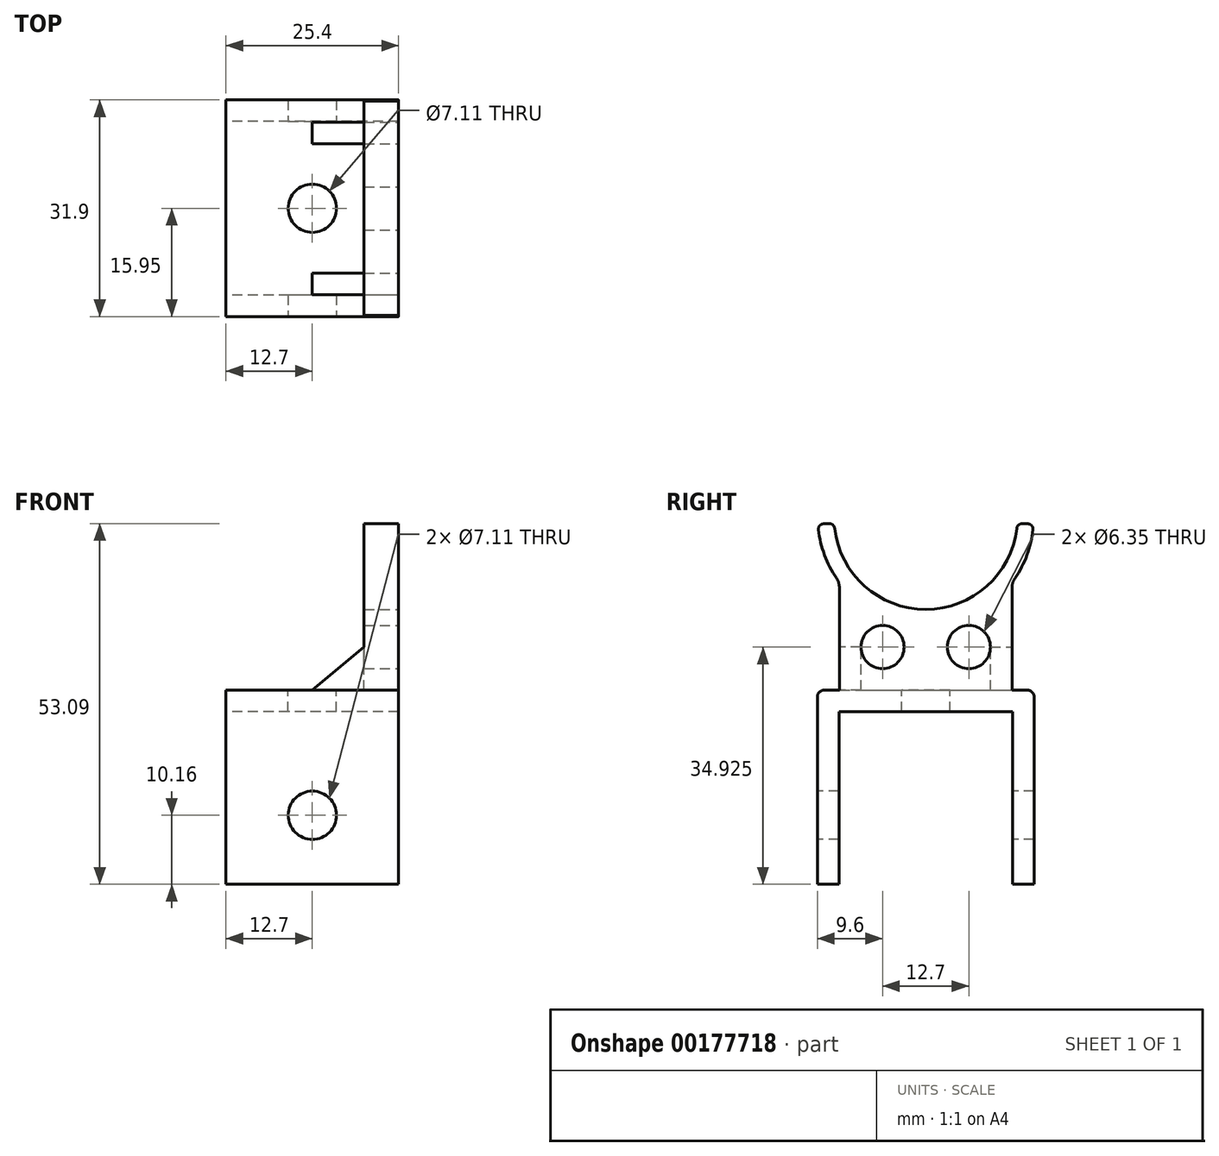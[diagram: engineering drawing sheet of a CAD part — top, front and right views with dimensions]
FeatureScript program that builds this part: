
annotation { "Feature Type Name" : "Feature", "Feature Type Description" : "" }
export const myFeature = defineFeature(function(context is Context, id is Id, definition is map)
    precondition{}
    {
        {
            var Q0;
            Q0=qCreatedBy(makeId("Right.planeOp"),FACE);
            var sketch = newSketch(context, id + "F0", { "sketchPlane" : qUnion([Q0])});
            skLineSegment(sketch, "E0.bottom", {"start": v(-12.78, 12.7) * mm, "end": v(12.78, 12.7) * mm});
            skLineSegment(sketch, "E0.left", {"start": v(-12.78, 12.7) * mm, "end": v(-12.78, -12.7) * mm});
            skLineSegment(sketch, "E0.right", {"start": v(12.78, 12.7) * mm, "end": v(12.78, -12.7) * mm});
            skLineSegment(sketch, "E1.0", {"start": v(15.95, 15.88) * mm, "end": v(15.95, -12.7) * mm});
            skLineSegment(sketch, "E2.0", {"start": v(-15.95, 15.87) * mm, "end": v(15.95, 15.88) * mm});
            skLineSegment(sketch, "E3.0", {"start": v(-15.95, 15.88) * mm, "end": v(-15.95, -12.7) * mm});
            skLineSegment(sketch, "E4", {"start": v(-15.95, -12.7) * mm, "end": v(-12.78, -12.7) * mm});
            skLineSegment(sketch, "E5", {"start": v(12.78, -12.7) * mm, "end": v(15.95, -12.7) * mm});
            skSolve(sketch);
        }
        {
            var Q0;
            Q0=makeQuery(id+"F0.imprint","IMPRINT",FACE,{"disambiguationData":[TD([[makeQuery(id+"F0.imprint","IMPRINT",EDGE,{"derivedFrom":sQuery(id+"F0.wireOp",EDGE,"E0.bottom")}),1.0]])]});
            extrude(context, id + "F1", {"entities" : qUnion([Q0]), "depth" : 25.4 * mm});
        }
        {
            var Q0;
            Q0=makeQuery(id+"F1.opExtrude","CAP_FACE",FACE,{"disambiguationData":[OSD([sQuery(id+"F0.wireOp",EDGE,"E0.bottom"),sQuery(id+"F0.wireOp",EDGE,"E0.left"),sQuery(id+"F0.wireOp",EDGE,"E0.right"),sQuery(id+"F0.wireOp",EDGE,"E1.0"),sQuery(id+"F0.wireOp",EDGE,"E2.0"),sQuery(id+"F0.wireOp",EDGE,"E3.0"),sQuery(id+"F0.wireOp",EDGE,"E4"),sQuery(id+"F0.wireOp",EDGE,"E5")])],"isStart":false});
            cPlane(context, id + "F2", {"entities" : qUnion([Q0]), "cplaneType" : CPlaneType.OFFSET, "offset" : 0 * mm, "width" : 152.4 * mm, "height" : 152.4 * mm});
        }
        {
            var Q0;
            Q0=qCreatedBy(id+"F2.planeOp",FACE);
            var sketch = newSketch(context, id + "F3", { "sketchPlane" : qUnion([Q0])});
            skPoint(sketch, "E6.0", {"position": v(0, 15.88) * mm});
            skLineSegment(sketch, "E7", {"start": v(0, 15.88) * mm, "end": v(0, 41.28) * mm, "construction": true});
            skArc(sketch, "E8", {"start": v(-13.4, 39.72) * mm, "mid": v(-8.98, 31.2) * mm, "end": v(0, 27.78) * mm});
            skLineSegment(sketch, "E9", {"start": v(-15.04, 40.37) * mm, "end": v(-14.18, 40.4) * mm});
            skPoint(sketch, "E10.visualSharp", {"position": v(-15.85, 40.36) * mm});
            skArc(sketch, "E10.filletArc", {"start": v(-15.04, 40.37) * mm, "mid": v(-15.6, 40.11) * mm, "end": v(-15.78, 39.53) * mm});
            skPoint(sketch, "E11.visualSharp", {"position": v(-13.47, 40.4) * mm});
            skArc(sketch, "E11.filletArc", {"start": v(-13.4, 39.72) * mm, "mid": v(-13.67, 40.2) * mm, "end": v(-14.18, 40.4) * mm});
            skLineSegment(sketch, "E12", {"start": v(-12.7, 15.88) * mm, "end": v(-12.7, 30.94) * mm});
            skArc(sketch, "E13", {"start": v(-15.78, 39.53) * mm, "mid": v(-14.9, 35.78) * mm, "end": v(-13.14, 32.36) * mm});
            skArc(sketch, "E14.MirrorCS", {"start": v(13.4, 39.72) * mm, "mid": v(8.98, 31.2) * mm, "end": v(0, 27.78) * mm});
            skLineSegment(sketch, "E15.MirrorCS", {"start": v(12.7, 15.88) * mm, "end": v(12.7, 30.94) * mm});
            skLineSegment(sketch, "E16.MirrorCS", {"start": v(15.04, 40.37) * mm, "end": v(14.18, 40.4) * mm});
            skArc(sketch, "E17.MirrorCS", {"start": v(13.4, 39.72) * mm, "mid": v(13.67, 40.2) * mm, "end": v(14.18, 40.4) * mm});
            skArc(sketch, "E18.MirrorCS", {"start": v(15.04, 40.37) * mm, "mid": v(15.6, 40.11) * mm, "end": v(15.78, 39.53) * mm});
            skArc(sketch, "E19.MirrorCS", {"start": v(15.78, 39.53) * mm, "mid": v(14.9, 35.78) * mm, "end": v(13.14, 32.36) * mm});
            skPoint(sketch, "E20.MirrorP", {"position": v(13.47, 40.4) * mm});
            skPoint(sketch, "E21.MirrorP", {"position": v(15.85, 40.36) * mm});
            skLineSegment(sketch, "E22", {"start": v(-12.7, 15.88) * mm, "end": v(12.7, 15.88) * mm});
            skPoint(sketch, "E23.visualSharp", {"position": v(-12.7, 31.75) * mm});
            skArc(sketch, "E23.filletArc", {"start": v(-12.7, 30.94) * mm, "mid": v(-12.81, 31.68) * mm, "end": v(-13.14, 32.36) * mm});
            skPoint(sketch, "E24.visualSharp", {"position": v(12.7, 31.75) * mm});
            skArc(sketch, "E24.filletArc", {"start": v(13.14, 32.36) * mm, "mid": v(12.81, 31.68) * mm, "end": v(12.7, 30.94) * mm});
            skCircle(sketch, "E25", {"center": v(-6.35, 22.23) * mm, "radius": 3.18 * mm});
            skCircle(sketch, "E26.MirrorC", {"center": v(6.35, 22.23) * mm, "radius": 3.18 * mm});
            skSolve(sketch);
        }
        {
            var Q0;
            Q0=makeQuery(id+"F3.imprint","IMPRINT",FACE,{"disambiguationData":[TD([[makeQuery(id+"F3.imprint","IMPRINT",EDGE,{"derivedFrom":sQuery(id+"F3.wireOp",EDGE,"E8")}),-1.0]])]});
            extrude(context, id + "F4", {"entities" : qUnion([Q0]), "operationType" : NewBodyOperationType.ADD, "oppositeDirection" : true, "depth" : 5.08 * mm});
        }
        {
            var Q0;
            Q0=makeQuery(id+"F1.opExtrude","SWEPT_FACE",FACE,{"disambiguationData":[OSD([sQuery(id+"F0.wireOp",EDGE,"E2.0")])]});
            cPlane(context, id + "F5", {"entities" : qUnion([Q0]), "cplaneType" : CPlaneType.OFFSET, "offset" : 0 * mm, "width" : 152.4 * mm, "height" : 152.4 * mm});
        }
        {
            var Q0;
            Q0=qCreatedBy(id+"F5.planeOp",FACE);
            var sketch = newSketch(context, id + "F6", { "sketchPlane" : qUnion([Q0])});
            skCircle(sketch, "E27", {"center": v(12.7, 0) * mm, "radius": 3.56 * mm});
            skSolve(sketch);
        }
        {
            var Q0;
            Q0 = qSketchRegion(id + "F6", true);
            extrude(context, id + "F7", {"entities" : qUnion([Q0]), "operationType" : NewBodyOperationType.REMOVE, "oppositeDirection" : true, "depth" : 6.35 * mm});
        }
        {
            var Q0;
            Q0=makeQuery(id+"F1.opExtrude","SWEPT_FACE",FACE,{"disambiguationData":[OSD([sQuery(id+"F0.wireOp",EDGE,"E3.0")])]});
            cPlane(context, id + "F8", {"entities" : qUnion([Q0]), "cplaneType" : CPlaneType.OFFSET, "offset" : 0 * mm, "width" : 152.4 * mm, "height" : 152.4 * mm});
        }
        {
            var Q0;
            Q0=qCreatedBy(id+"F8.planeOp",FACE);
            var sketch = newSketch(context, id + "F9", { "sketchPlane" : qUnion([Q0])});
            skCircle(sketch, "E28", {"center": v(12.7, -2.54) * mm, "radius": 3.56 * mm});
            skSolve(sketch);
        }
        {
            var Q0;
            Q0 = qSketchRegion(id + "F9", true);
            extrude(context, id + "F10", {"entities" : qUnion([Q0]), "operationType" : NewBodyOperationType.REMOVE, "endBound" : BoundingType.THROUGH_ALL, "oppositeDirection" : true, "depth" : 25.4 * mm});
        }
        {
            var Q0;
            Q0=makeQuery(id+"F4.opExtrude","SWEPT_FACE",FACE,{"disambiguationData":[OSD([sQuery(id+"F3.wireOp",EDGE,"E12")])]});
            cPlane(context, id + "F11", {"entities" : qUnion([Q0]), "cplaneType" : CPlaneType.OFFSET, "offset" : 0 * mm, "width" : 152.4 * mm, "height" : 152.4 * mm});
        }
        {
            var Q0;
            Q0=qCreatedBy(id+"F11.planeOp",FACE);
            var sketch = newSketch(context, id + "F12", { "sketchPlane" : qUnion([Q0])});
            skLineSegment(sketch, "E29.0", {"start": v(20.32, 15.88) * mm, "end": v(20.32, 30.94) * mm, "construction": true});
            skLineSegment(sketch, "E30", {"start": v(20.32, 15.88) * mm, "end": v(20.32, 22.23) * mm});
            skLineSegment(sketch, "E31", {"start": v(20.32, 15.88) * mm, "end": v(12.7, 15.88) * mm});
            skLineSegment(sketch, "E32", {"start": v(12.7, 15.88) * mm, "end": v(20.32, 22.23) * mm});
            skSolve(sketch);
        }
        {
            var Q0;
            Q0 = qSketchRegion(id + "F12", true);
            extrude(context, id + "F13", {"entities" : qUnion([Q0]), "oppositeDirection" : true, "depth" : 3.17 * mm});
        }
        {
            var Q0;
            Q0=makeQuery(id+"F13.opExtrude","SWEPT_BODY",BODY,{"disambiguationData":[OSD([sQuery(id+"F12.wireOp",EDGE,"E30"),sQuery(id+"F12.wireOp",EDGE,"E31"),sQuery(id+"F12.wireOp",EDGE,"E32")])]});
            var Q1;
            Q1=qCreatedBy(makeId("Front.planeOp"),FACE);
            mirror(context, id + "F14", {"operationType" : NewBodyOperationType.ADD, "entities" : qUnion([Q0]), "mirrorPlane" : qUnion([Q1])});
        }
        {
            var Q0;
            Q0=makeQuery(id+"F1.opExtrude","SWEPT_EDGE",EDGE,{"disambiguationData":[OSD([sQuery(id+"F0.wireOp",EDGE,"E2.0"),sQuery(id+"F0.wireOp",EDGE,"E3.0")])]});
            var Q1;
            Q1=makeQuery(id+"F1.opExtrude","SWEPT_EDGE",EDGE,{"disambiguationData":[OSD([sQuery(id+"F0.wireOp",EDGE,"E1.0"),sQuery(id+"F0.wireOp",EDGE,"E2.0")])]});
            var Q2;
            Q2=makeQuery(id+"F4.opExtrude","CAP_EDGE",EDGE,{"disambiguationData":[OSD([sQuery(id+"F3.wireOp",EDGE,"E22")])],"isStart":false});
            var Q3;
            Q3=makeQuery(id+"F14.opPattern","COPY",EDGE,{"derivedFrom":makeQuery(id+"F13.opExtrude","CAP_EDGE",EDGE,{"disambiguationData":[OSD([sQuery(id+"F12.wireOp",EDGE,"E31")])],"isStart":false}),"instanceName":"1"});
            var Q4;
            Q4=makeQuery(id+"F13.opExtrude","CAP_EDGE",EDGE,{"disambiguationData":[OSD([sQuery(id+"F12.wireOp",EDGE,"E31")])],"isStart":false});
            var Q5;
            Q5=makeQuery(id+"F14.boolean.opBoolean","MERGE",EDGE,{"derivedFrom":[makeQuery(id+"F4.opExtrude","SWEPT_EDGE",EDGE,{"disambiguationData":[OSD([sQuery(id+"F3.wireOp",EDGE,"E15.MirrorCS"),sQuery(id+"F3.wireOp",EDGE,"E22")])]}),makeQuery(id+"F14.opPattern","COPY",EDGE,{"derivedFrom":makeQuery(id+"F13.opExtrude","CAP_EDGE",EDGE,{"disambiguationData":[OSD([sQuery(id+"F12.wireOp",EDGE,"E31")])],"isStart":true}),"instanceName":"1"})]});
            var Q6;
            Q6=makeQuery(id+"F14.opPattern","COPY",EDGE,{"derivedFrom":makeQuery(id+"F13.opExtrude","SWEPT_EDGE",EDGE,{"disambiguationData":[OSD([sQuery(id+"F12.wireOp",EDGE,"E31"),sQuery(id+"F12.wireOp",EDGE,"E32")])]}),"instanceName":"1"});
            var Q7;
            Q7=makeQuery(id+"F13.opExtrude","SWEPT_EDGE",EDGE,{"disambiguationData":[OSD([sQuery(id+"F12.wireOp",EDGE,"E31"),sQuery(id+"F12.wireOp",EDGE,"E32")])]});
            var Q8;
            Q8=makeQuery(id+"F14.boolean.opBoolean","MERGE",EDGE,{"derivedFrom":[makeQuery(id+"F4.opExtrude","SWEPT_EDGE",EDGE,{"disambiguationData":[OSD([sQuery(id+"F3.wireOp",EDGE,"E12"),sQuery(id+"F3.wireOp",EDGE,"E22")])]}),makeQuery(id+"F13.opExtrude","CAP_EDGE",EDGE,{"disambiguationData":[OSD([sQuery(id+"F12.wireOp",EDGE,"E31")])],"isStart":true})]});
            var Q9;
            Q9=makeQuery(id+"F14.opPattern","COPY",EDGE,{"derivedFrom":makeQuery(id+"F13.opExtrude","SWEPT_EDGE",EDGE,{"disambiguationData":[OSD([sQuery(id+"F12.wireOp",EDGE,"E30"),sQuery(id+"F12.wireOp",EDGE,"E32")])]}),"instanceName":"1"});
            var Q10;
            Q10=makeQuery(id+"F13.opExtrude","SWEPT_EDGE",EDGE,{"disambiguationData":[OSD([sQuery(id+"F12.wireOp",EDGE,"E30"),sQuery(id+"F12.wireOp",EDGE,"E32")])]});
            fillet(context, id + "F15", {"entities" : qUnion([Q0, Q1, Q2, Q3, Q4, Q5, Q6, Q7, Q8, Q9, Q10]), "radius" : 1.02 * mm, "tangentPropagation" : true, "allowEdgeOverflow" : false});
        }
    });
